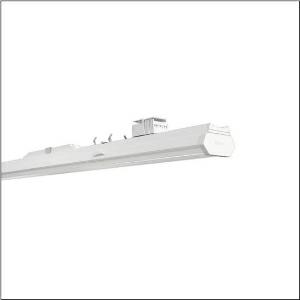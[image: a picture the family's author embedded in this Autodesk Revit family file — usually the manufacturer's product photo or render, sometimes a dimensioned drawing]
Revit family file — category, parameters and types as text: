
# Revit family: licross_r__21_protected_mo_52tp127n38xg_ec59
name_source: partatom
category: Lighting Fixtures
units: mm (PartAtom-declared; Revit-internal decimal feet)

## family parameters
Cut with Voids When Loaded = No
Host = Face
Light Source = No
Part Type = Normal
Room Calculation Point = No
Round Connector Dimension = Use Diameter
Shared = No

## types (1)
- Licross® 21 Protected MO (1 x LED, 8080 lm, 47.9 W, 3000K)
    Apparent Load = 48 VA
    CIE Flux Codes = 73 92 98 99 100
    Color Rendering = 80
    Color Temperature = 3000K
    Default Elevation = 1800 mm
    Description = Licross® 21 Protected MO, luminaire insert, of sheet steel, galvanised, coil coated, white, length: 1.500mm, width: 90mm, height: 101mm, LED rated luminous flux: 8.080lm, light colour: 830, control gear: ON/OFF, with plug, 3-pole, with phase selection, mains connection: 220..240V, AC, 50/60Hz, rated input power: 48W, halogen-free wiring, primary light control with lens, of plastic, primary optical cover: cover, of PMMA, light emission: direct distribution, primary light characteristic: symmetric, protection rating (complete): IP64, insulation class (complete): insulation class I (protective earthing), certification: CE, ENEC, VDE, UKCA, protection symbol: D if used in an environment with conductive dust loads with corresponding accessories, impact resistance: IK06, permissible ambient temperature for indoor applications: -35..+45°C, corresponds to IFS (International Featured Standards) requirements for safety and quality in the food industry, reducing of maximum allowable ambient temperature of 5°C with ceiling mounting, LABS conformity tested according to VDMA 24364:2018-05, packaging unit: 1 piece
    Height = 92 mm
    Lamp = 1 x LED
    Lamp Light Flux = 8080 lm
    Lamp Power = 47.9 W
    Lamp count = 1
    Length = 1500 mm
    Luminous efficacy = 169 lm/W
    Manufacturer = Siteco
    ModVariant = No
    Model = 52TP127N38XG
    Mounting Place = Ceiling
    Mounting Type = Pendant
    Number of Poles = 1
    OnlyDefault = Yes
    Power Factor = 1
    Product Name = Licross® 21 Protected MO
    Product group = luminaire insert
    ProductGroupID = 902
    Protection Class = Protection class I
    Protection Degree = IP 64
    RLX_Detail_Level = 1
    RLX_Emergency_Light_Flux = 0 lm
    RLX_Emergency_Type = 0
    RLX_Emergency_Type_DB = No
    RlxData = <blob elided: 20717 chars, md5=b2b34efb>
    Socket = socket
    Standby Power = 0 W
    System Light Flux = 8080 lm
    System Power = 48 W
    Type Comments = Product without accessories
    Type Image = l_1256148.jpg
    URL = http://relux.com
    VarID = ---
    Voltage = 0 V
    Weight = 0.00 kg
    Width = 88 mm

## geometry (parser evidence)
native form markers: Blend x4, Sweep x12
no freeform markers — native parametric forms only
